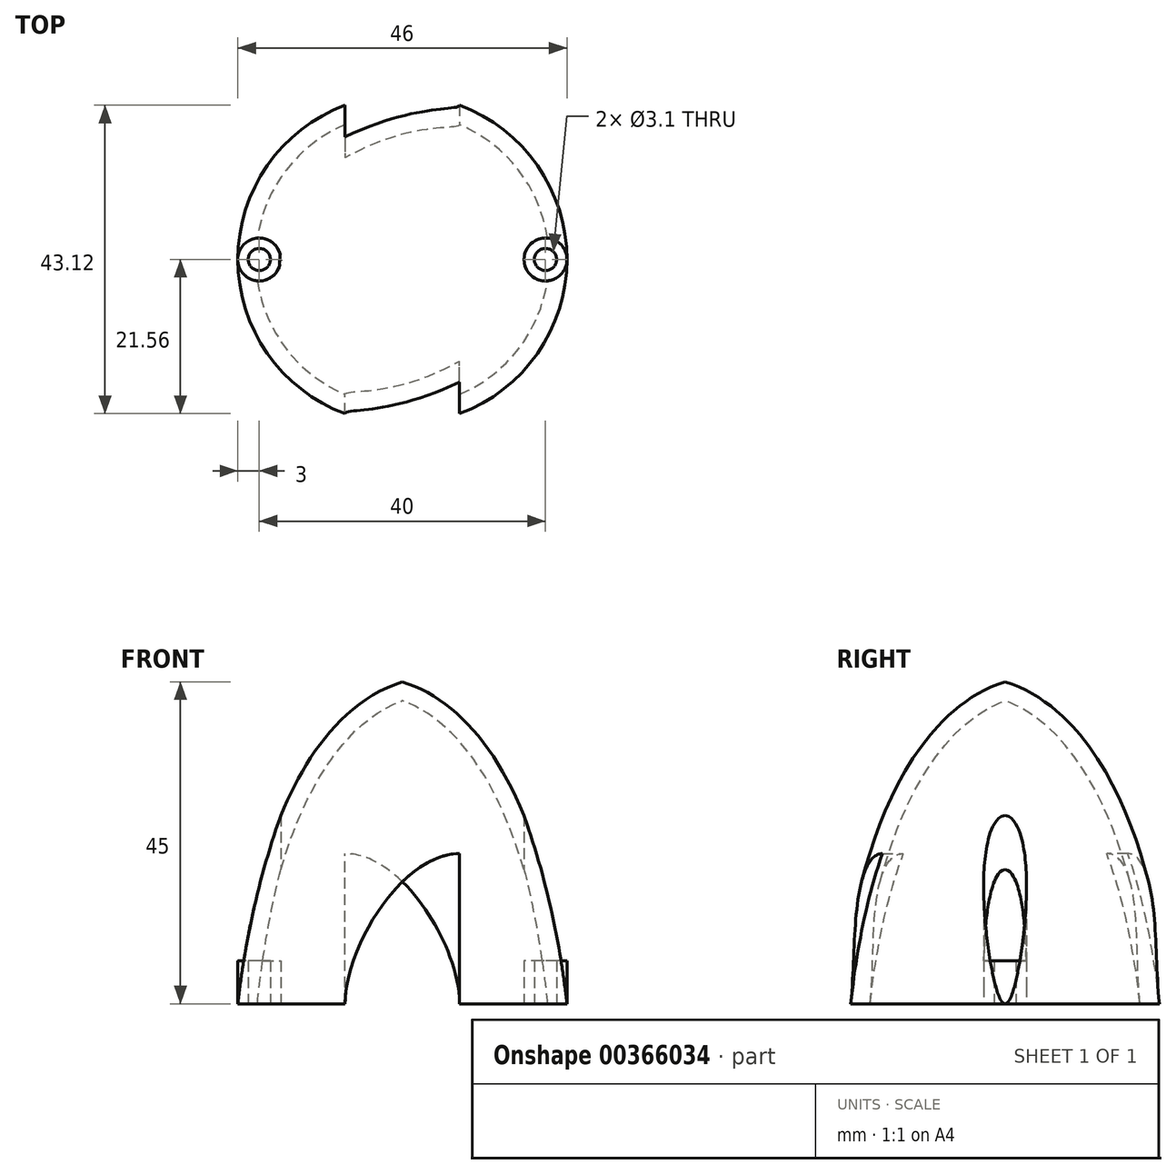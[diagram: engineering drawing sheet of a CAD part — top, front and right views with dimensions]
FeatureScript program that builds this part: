
annotation { "Feature Type Name" : "Feature", "Feature Type Description" : "" }
export const myFeature = defineFeature(function(context is Context, id is Id, definition is map)
    precondition{}
    {
        {
            var Q0;
            Q0=qCreatedBy(makeId("Front.planeOp"),FACE);
            var sketch = newSketch(context, id + "F0", { "sketchPlane" : qUnion([Q0])});
            skLineSegment(sketch, "E0", {"start": v(0, 0) * mm, "end": v(23, 0) * mm});
            skFitSpline(sketch, "E1", {"points": [v(23, 0) * mm, v(0, 45) * mm], "startDerivative": vector(-7.55, 76.93) * mm, "endDerivative": vector(-35.05, 10.73) * mm});
            skLineSegment(sketch, "E2", {"start": v(0, 0) * mm, "end": v(0, 45) * mm});
            skLineSegment(sketch, "E3", {"start": v(0, 63.88) * mm, "end": v(0, -31.1) * mm, "construction": true});
            skSolve(sketch);
        }
        {
            var Q0;
            Q0=qSketchRegion(id+"F0",true);
            var Q1;
            Q1=sQuery(id+"F0.wireOp",EDGE,"E3");
            revolve(context, id + "F1", {"entities" : qUnion([Q0]), "axis" : qUnion([Q1]), "revolveType" : RevolveType.FULL});
        }
        {
            var Q0;
            Q0=makeQuery(id+"F1.opRevolve","SWEPT_FACE",FACE,{"disambiguationData":[OSD([sQuery(id+"F0.wireOp",EDGE,"E0")])]});
            shell(context, id + "F2", {"entities" : qUnion([Q0]), "thickness" : 2.5 * mm});
        }
        {
            var Q0;
            Q0=qCreatedBy(makeId("Top.planeOp"),FACE);
            var sketch = newSketch(context, id + "F3", { "sketchPlane" : qUnion([Q0])});
            skCircle(sketch, "E4", {"center": v(-20, 0) * mm, "radius": 3 * mm});
            skCircle(sketch, "E5", {"center": v(-20, 0) * mm, "radius": 1.55 * mm});
            skCircle(sketch, "E6.MirrorC", {"center": v(20, 0) * mm, "radius": 3 * mm});
            skCircle(sketch, "E7.MirrorC", {"center": v(20, 0) * mm, "radius": 1.55 * mm});
            skSolve(sketch);
        }
        {
            var Q0;
            Q0=qSketchRegion(id+"F3",true);
            extrude(context, id + "F4", {"entities" : qUnion([Q0]), "operationType" : NewBodyOperationType.ADD, "depth" : 6 * mm});
        }
        {
            var Q0;
            {var subQ0=sQuery(id+"F3.wireOp",EDGE,"E4");Q0=makeQuery(id+"F4.boolean.opBoolean","SPLIT",FACE,{"disambiguationData":[TD([makeQuery(id+"F1.opRevolve","SWEPT_FACE",FACE,{"disambiguationData":[OSD([sQuery(id+"F0.wireOp",EDGE,"E1")])]})])],"derivedFrom":makeQuery(id+"F4.opExtrude","CAP_FACE",FACE,{"disambiguationData":[OSD([subQ0,sQuery(id+"F3.wireOp",EDGE,"E5")])],"isStart":false})});}
            var sketch = newSketch(context, id + "F5", { "sketchPlane" : qUnion([Q0])});
            skCircle(sketch, "E8", {"center": v(-20, 0) * mm, "radius": 3 * mm});
            skCircle(sketch, "E9.MirrorC", {"center": v(20, 0) * mm, "radius": 3 * mm});
            skSolve(sketch);
        }
        {
            var Q0;
            Q0=qSketchRegion(id+"F5",true);
            extrude(context, id + "F6", {"entities" : qUnion([Q0]), "operationType" : NewBodyOperationType.REMOVE, "depth" : 25 * mm});
        }
        {
            var Q0;
            {var subQ0=sQuery(id+"F0.wireOp",EDGE,"E1");var subQ1=sQuery(id+"F3.wireOp",EDGE,"E4");var subQ3=sQuery(id+"F3.wireOp",EDGE,"E5");var subQ4=makeQuery(id+"F4.opExtrude","CAP_FACE",FACE,{"disambiguationData":[OSD([subQ1,subQ3])],"isStart":false});Q0=makeQuery(id+"F6.boolean.opBoolean","MERGE",FACE,{"derivedFrom":[makeQuery(id+"F4.boolean.opBoolean","SPLIT",FACE,{"disambiguationData":[TD([makeQuery(id+"F1.opRevolve","SWEPT_FACE",FACE,{"disambiguationData":[OSD([subQ0])]})])],"derivedFrom":subQ4}),makeQuery(id+"F4.boolean.opBoolean","SPLIT",FACE,{"disambiguationData":[TD([makeQuery(id+"F2.opShell","OFFSET_FACE",FACE,{"disambiguationData":[OSD([subQ0])]})])],"derivedFrom":subQ4}),makeQuery(id+"F6.opExtrude","CAP_FACE",FACE,{"disambiguationData":[OSD([sQuery(id+"F5.wireOp",EDGE,"E8")])],"isStart":true})]});}
            var sketch = newSketch(context, id + "F7", { "sketchPlane" : qUnion([Q0])});
            skCircle(sketch, "E10", {"center": v(-20, 0) * mm, "radius": 1.55 * mm});
            skCircle(sketch, "E11.MirrorC", {"center": v(20, 0) * mm, "radius": 1.55 * mm});
            skSolve(sketch);
        }
        {
            var Q0;
            Q0=qSketchRegion(id+"F7",true);
            extrude(context, id + "F8", {"entities" : qUnion([Q0]), "operationType" : NewBodyOperationType.REMOVE, "oppositeDirection" : true, "depth" : 25 * mm});
        }
        {
            var Q0;
            Q0=qCreatedBy(makeId("Front.planeOp"),FACE);
            var sketch = newSketch(context, id + "F9", { "sketchPlane" : qUnion([Q0])});
            skLineSegment(sketch, "E12", {"start": v(-8, 0) * mm, "end": v(8, 0) * mm});
            skLineSegment(sketch, "E13", {"start": v(8, 0) * mm, "end": v(8, 21) * mm});
            skFitSpline(sketch, "E14", {"points": [v(-8, 0) * mm, v(8, 21) * mm], "startDerivative": vector(0, 24) * mm, "endDerivative": vector(24, 0) * mm});
            skSolve(sketch);
        }
        {
            var Q0;
            Q0=qSketchRegion(id+"F9",true);
            extrude(context, id + "F10", {"entities" : qUnion([Q0]), "operationType" : NewBodyOperationType.REMOVE, "endBound" : BoundingType.THROUGH_ALL, "depth" : 50 * mm});
        }
        {
            var Q0;
            Q0=qCreatedBy(makeId("Front.planeOp"),FACE);
            var sketch = newSketch(context, id + "F11", { "sketchPlane" : qUnion([Q0])});
            skLineSegment(sketch, "E15", {"start": v(-8, 0) * mm, "end": v(-8, 21) * mm});
            skLineSegment(sketch, "E16.MirrorCS", {"start": v(8, 0) * mm, "end": v(-8, 0) * mm});
            skFitSpline(sketch, "E17.MirrorCS", {"points": [v(8, 0) * mm, v(-8, 21) * mm], "startDerivative": vector(0, 24) * mm, "endDerivative": vector(-24, 0) * mm});
            skSolve(sketch);
        }
        {
            var Q0;
            Q0 = qSketchRegion(id + "F11", true);
            extrude(context, id + "F12", {"entities" : qUnion([Q0]), "operationType" : NewBodyOperationType.REMOVE, "endBound" : BoundingType.THROUGH_ALL, "oppositeDirection" : true, "depth" : 25 * mm});
        }
    });
